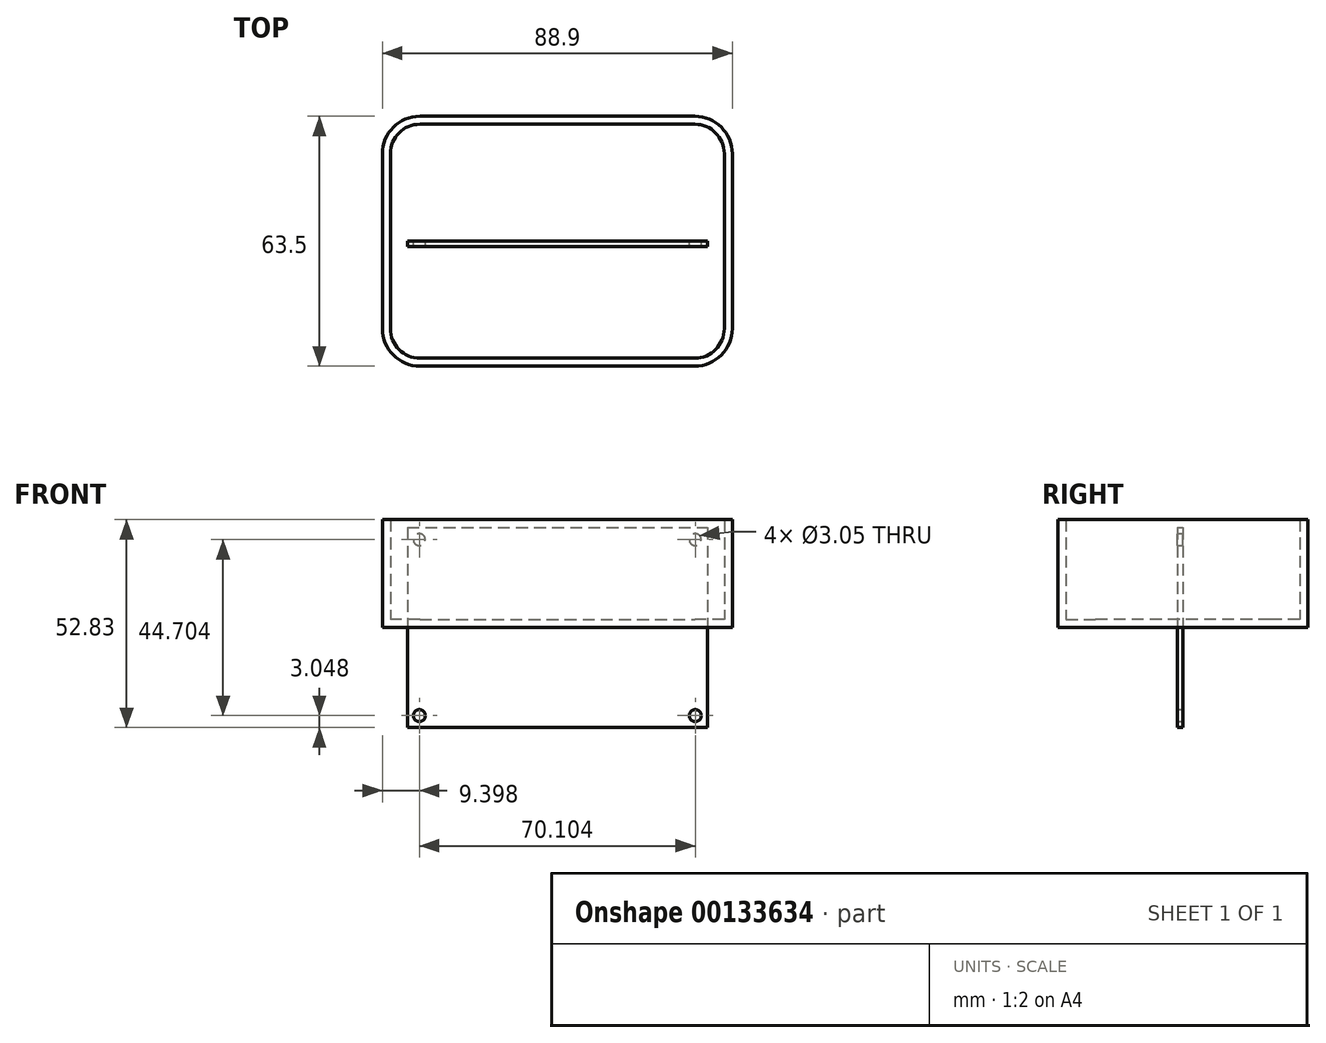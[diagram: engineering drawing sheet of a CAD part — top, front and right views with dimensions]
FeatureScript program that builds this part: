
annotation { "Feature Type Name" : "Feature", "Feature Type Description" : "" }
export const myFeature = defineFeature(function(context is Context, id is Id, definition is map)
    precondition{}
    {
        {
            var Q0;
            Q0=qCreatedBy(makeId("Front.planeOp"),FACE);
            var sketch = newSketch(context, id + "F0", { "sketchPlane" : qUnion([Q0])});
            skPoint(sketch, "E0.middle", {"position": v(0, 0) * mm});
            skLineSegment(sketch, "E1.bottom", {"start": v(-35.05, 22.35) * mm, "end": v(35.05, 22.35) * mm, "construction": true});
            skLineSegment(sketch, "E1.top", {"start": v(-35.05, -22.35) * mm, "end": v(35.05, -22.35) * mm, "construction": true});
            skLineSegment(sketch, "E1.left", {"start": v(-35.05, 22.35) * mm, "end": v(-35.05, -22.35) * mm, "construction": true});
            skLineSegment(sketch, "E1.right", {"start": v(35.05, 22.35) * mm, "end": v(35.05, -22.35) * mm, "construction": true});
            skCircle(sketch, "E2", {"center": v(-35.05, 22.35) * mm, "radius": 1.52 * mm});
            skCircle(sketch, "E3", {"center": v(35.05, 22.35) * mm, "radius": 1.52 * mm});
            skCircle(sketch, "E4", {"center": v(35.05, -22.35) * mm, "radius": 1.52 * mm});
            skCircle(sketch, "E5", {"center": v(-35.05, -22.35) * mm, "radius": 1.52 * mm});
            skLineSegment(sketch, "E6.bottom", {"start": v(-38.1, 25.4) * mm, "end": v(38.1, 25.4) * mm});
            skLineSegment(sketch, "E6.top", {"start": v(-38.1, -25.4) * mm, "end": v(38.1, -25.4) * mm});
            skLineSegment(sketch, "E6.left", {"start": v(-38.1, 25.4) * mm, "end": v(-38.1, -25.4) * mm});
            skLineSegment(sketch, "E6.right", {"start": v(38.1, 25.4) * mm, "end": v(38.1, -25.4) * mm});
            skSolve(sketch);
        }
        {
            var Q0;
            Q0=makeQuery(id+"F0.imprint","IMPRINT",FACE,{"disambiguationData":[TD([[makeQuery(id+"F0.imprint","IMPRINT",EDGE,{"derivedFrom":sQuery(id+"F0.wireOp",EDGE,"E2")}),-1.0]])]});
            extrude(context, id + "F1", {"entities" : qUnion([Q0]), "depth" : 1.4 * mm});
        }
        {
            var Q0;
            Q0=qCreatedBy(makeId("Top.planeOp"),FACE);
            var sketch = newSketch(context, id + "F2", { "sketchPlane" : qUnion([Q0])});
            skLineSegment(sketch, "E7.bottom", {"start": v(-38.1, 25.4) * mm, "end": v(38.1, 25.4) * mm, "construction": true});
            skLineSegment(sketch, "E7.top", {"start": v(-38.1, -25.4) * mm, "end": v(38.1, -25.4) * mm, "construction": true});
            skLineSegment(sketch, "E7.left", {"start": v(-38.1, 25.4) * mm, "end": v(-38.1, -25.4) * mm, "construction": true});
            skLineSegment(sketch, "E7.right", {"start": v(38.1, 25.4) * mm, "end": v(38.1, -25.4) * mm, "construction": true});
            skPoint(sketch, "E7.middle", {"position": v(0, 0) * mm});
            skLineSegment(sketch, "E8.bottom", {"start": v(-44.45, 31.75) * mm, "end": v(44.45, 31.75) * mm});
            skLineSegment(sketch, "E8.top", {"start": v(-44.45, -31.75) * mm, "end": v(44.45, -31.75) * mm});
            skLineSegment(sketch, "E8.left", {"start": v(-44.45, 31.75) * mm, "end": v(-44.45, -31.75) * mm});
            skLineSegment(sketch, "E8.right", {"start": v(44.45, 31.75) * mm, "end": v(44.45, -31.75) * mm});
            skSolve(sketch);
        }
        {
            var Q0;
            Q0 = qSketchRegion(id + "F2", true);
            extrude(context, id + "F3", {"entities" : qUnion([Q0]), "depth" : 2.03 * mm});
        }
        {
            var Q0;
            Q0=makeQuery(id+"F3.opExtrude","SWEPT_EDGE",EDGE,{"disambiguationData":[OSD([sQuery(id+"F2.wireOp",EDGE,"E8.top"),sQuery(id+"F2.wireOp",EDGE,"E8.left")])]});
            var Q1;
            Q1=makeQuery(id+"F3.opExtrude","SWEPT_EDGE",EDGE,{"disambiguationData":[OSD([sQuery(id+"F2.wireOp",EDGE,"E8.top"),sQuery(id+"F2.wireOp",EDGE,"E8.right")])]});
            var Q2;
            Q2=makeQuery(id+"F3.opExtrude","SWEPT_EDGE",EDGE,{"disambiguationData":[OSD([sQuery(id+"F2.wireOp",EDGE,"E8.bottom"),sQuery(id+"F2.wireOp",EDGE,"E8.left")])]});
            var Q3;
            Q3=makeQuery(id+"F3.opExtrude","SWEPT_EDGE",EDGE,{"disambiguationData":[OSD([sQuery(id+"F2.wireOp",EDGE,"E8.bottom"),sQuery(id+"F2.wireOp",EDGE,"E8.right")])]});
            fillet(context, id + "F4", {"entities" : qUnion([Q0, Q1, Q2, Q3]), "radius" : 9.52 * mm, "tangentPropagation" : true, "allowEdgeOverflow" : false});
        }
        {
            var Q0;
            Q0=makeQuery(id+"F3.opExtrude","CAP_FACE",FACE,{"disambiguationData":[OSD([sQuery(id+"F2.wireOp",EDGE,"E8.bottom"),sQuery(id+"F2.wireOp",EDGE,"E8.top"),sQuery(id+"F2.wireOp",EDGE,"E8.left"),sQuery(id+"F2.wireOp",EDGE,"E8.right")])],"isStart":false});
            var sketch = newSketch(context, id + "F5", { "sketchPlane" : qUnion([Q0])});
            skPoint(sketch, "E9.visualSharp", {"position": v(-42.42, 29.72) * mm});
            skPoint(sketch, "E10.visualSharp", {"position": v(42.42, 29.72) * mm});
            skPoint(sketch, "E11.visualSharp", {"position": v(42.42, -29.72) * mm});
            skPoint(sketch, "E12.visualSharp", {"position": v(-42.42, -29.72) * mm});
            skLineSegment(sketch, "E13.0", {"start": v(-34.93, 31.75) * mm, "end": v(34.93, 31.75) * mm});
            skArc(sketch, "E13.1", {"start": v(44.45, 22.23) * mm, "mid": v(41.66, 28.96) * mm, "end": v(34.93, 31.75) * mm});
            skArc(sketch, "E13.2", {"start": v(-34.93, 31.75) * mm, "mid": v(-41.66, 28.96) * mm, "end": v(-44.45, 22.23) * mm});
            skLineSegment(sketch, "E13.3", {"start": v(44.45, 22.23) * mm, "end": v(44.45, -22.23) * mm});
            skLineSegment(sketch, "E13.4", {"start": v(-44.45, 22.23) * mm, "end": v(-44.45, -22.23) * mm});
            skArc(sketch, "E13.5", {"start": v(-44.45, -22.23) * mm, "mid": v(-41.66, -28.96) * mm, "end": v(-34.93, -31.75) * mm});
            skLineSegment(sketch, "E13.6", {"start": v(-34.93, -31.75) * mm, "end": v(34.93, -31.75) * mm});
            skArc(sketch, "E13.7", {"start": v(44.45, -22.23) * mm, "mid": v(41.66, -28.96) * mm, "end": v(34.93, -31.75) * mm});
            skLineSegment(sketch, "E14.0", {"start": v(-34.93, 29.72) * mm, "end": v(34.93, 29.72) * mm});
            skArc(sketch, "E14.1", {"start": v(42.42, 22.23) * mm, "mid": v(40.22, 27.52) * mm, "end": v(34.93, 29.72) * mm});
            skArc(sketch, "E14.2", {"start": v(-34.93, 29.72) * mm, "mid": v(-40.22, 27.52) * mm, "end": v(-42.42, 22.23) * mm});
            skLineSegment(sketch, "E14.3", {"start": v(42.42, 22.23) * mm, "end": v(42.42, -22.23) * mm});
            skLineSegment(sketch, "E14.4", {"start": v(-42.42, 22.23) * mm, "end": v(-42.42, -22.23) * mm});
            skArc(sketch, "E14.5", {"start": v(-42.42, -22.23) * mm, "mid": v(-40.22, -27.52) * mm, "end": v(-34.93, -29.72) * mm});
            skLineSegment(sketch, "E14.6", {"start": v(-34.93, -29.72) * mm, "end": v(34.93, -29.72) * mm});
            skArc(sketch, "E14.7", {"start": v(42.42, -22.23) * mm, "mid": v(40.22, -27.52) * mm, "end": v(34.93, -29.72) * mm});
            skSolve(sketch);
        }
        {
            var Q0;
            Q0 = qSketchRegion(id + "F5", true);
            extrude(context, id + "F6", {"entities" : qUnion([Q0]), "operationType" : NewBodyOperationType.ADD, "depth" : 25.4 * mm});
        }
    });
